# Revit family: Trane_TVR_Outdoor_4TVH0086(96)EE000AA_380~415V(50_60Hz)
name_source: partatom
category: Equipamento mecânico
units: mm (PartAtom-declared; Revit-internal decimal feet)

## family parameters
Com base no plano de trabalho = Não
Compartilhado = Não
Corte com vazios quando carregada = Não
Cota do conector redondo = Utilizar diâmetro
Número OmniClass = 23.75.00.00
Ponto de cálculo do ambiente = Não
Sempre na vertical = Sim
Tipo de parte = Normal
Título OmniClass = Climate Control (HVAC)

## types (2) — shared parameters
Air Flow = 11000.000 m³/h
Casing color = White
Compressor = 1
Condensation = Air
Depth = 790  [stored 2.59186 ft]
Descrição = High efficiency air cooled
Fabricante = Trane
Gas = R410A
Gas pipe = 25.4  [stored 0.0833333 ft]
Height = 1635  [stored 5.36417 ft]
Installation = Outdoor installation
Liquid pipe = 12.7  [stored 0.0416667 ft]
Machine material = Galvanized Steel
Maximum Fuse Amps = 32 A
Net Weight = 227.00 kg
Power supply = 380V 3Ph~60Hz
Series = ULTRA
URL = https://www.trane.com
Width = 990  [stored 3.24803 ft]
clearance access behind = 1000  [stored 3.28084 ft]
clearance access front = 1000  [stored 3.28084 ft]
clearance access left = 1000  [stored 3.28084 ft]
clearance access right = 1000  [stored 3.28084 ft]

## per-type parameters (varying)
| type | Cooling Capacity | Cooling Power Input | Heating Capacity | Heating Power Input | Minimum Circuit Amps |
| 4TVH0086EE000AA | 25.200 kW | 4.800 kW | 25.200 kW | 4.560 kW | 24 A |
| 4TVH0096EE000AA | 28.000 kW | 5.700 kW | 28.000 kW | 5.120 kW | 25 A |

note: column(s) folded — value = type name in every type: Modelo

note: [stored X ft] marks values corroborated as IEEE doubles in the binary element streams (Revit-internal decimal feet)

## geometry (parser evidence)
native form markers: Sweep x17
no freeform markers — native parametric forms only
